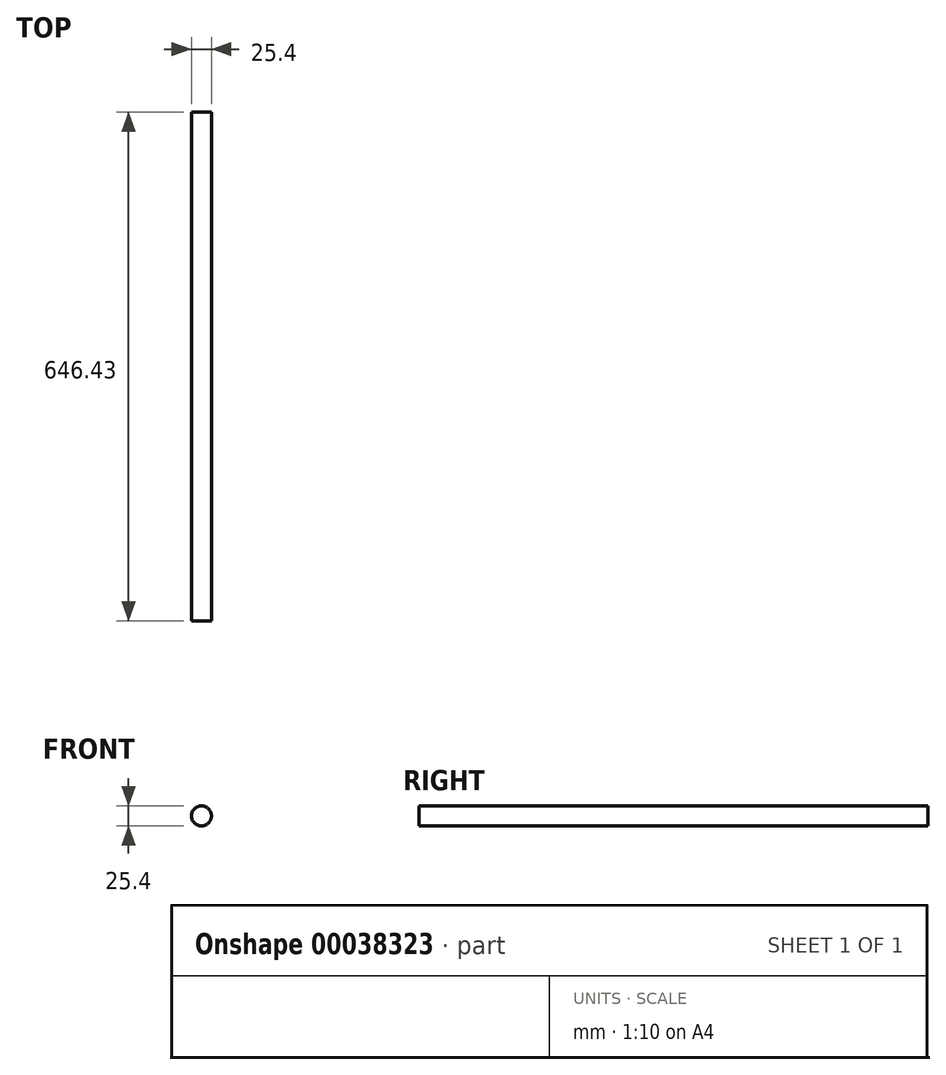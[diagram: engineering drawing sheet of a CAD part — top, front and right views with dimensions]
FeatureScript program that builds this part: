
annotation { "Feature Type Name" : "Feature", "Feature Type Description" : "" }
export const myFeature = defineFeature(function(context is Context, id is Id, definition is map)
    precondition{}
    {
        {
            var Q0;
            Q0=qCreatedBy(makeId("Front.planeOp"),FACE);
            var sketch = newSketch(context, id + "F0", { "sketchPlane" : qUnion([Q0])});
            skCircle(sketch, "E0", {"center": v(-61.75, 56.03) * mm, "radius": 12.7 * mm});
            skLineSegment(sketch, "E1", {"start": v(-203.1, 89.57) * mm, "end": v(-165, 89.57) * mm});
            skLineSegment(sketch, "E2", {"start": v(-165, 89.57) * mm, "end": v(-165, 127.67) * mm});
            skLineSegment(sketch, "E3", {"start": v(-203.1, 89.57) * mm, "end": v(-165, 127.67) * mm});
            skSolve(sketch);
        }
        {
            var Q0;
            Q0=makeQuery(id+"F0.imprint","IMPRINT",FACE,{"disambiguationData":[TD([[makeQuery(id+"F0.imprint","IMPRINT",EDGE,{"derivedFrom":sQuery(id+"F0.wireOp",EDGE,"E0")}),1.0]])]});
            extrude(context, id + "F1", {"entities" : qUnion([Q0]), "depth" : 646.43 * mm});
        }
    });
